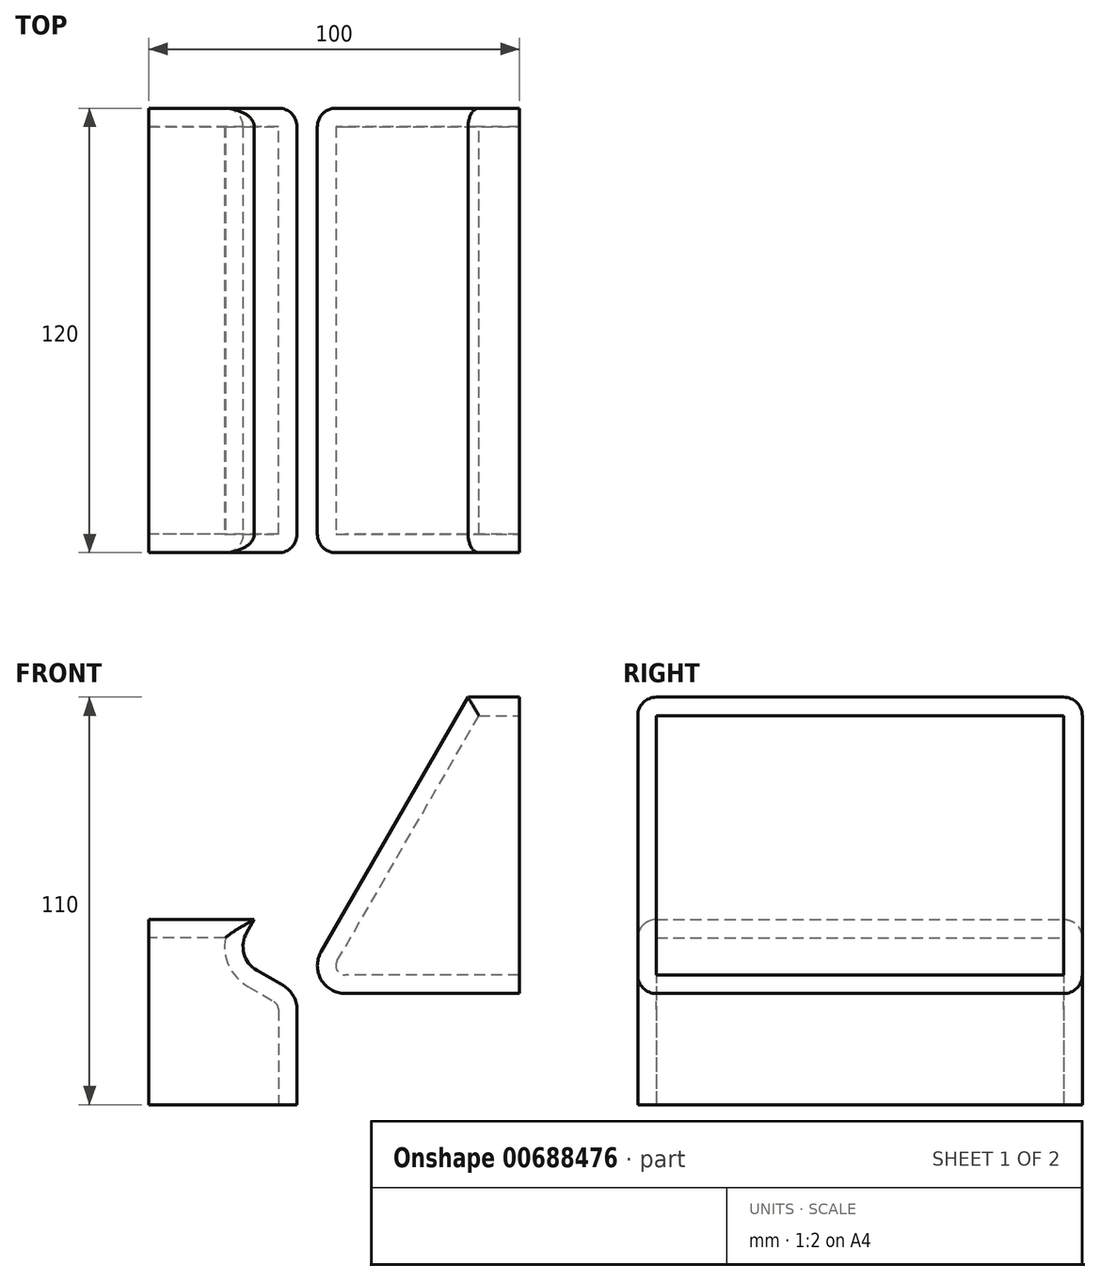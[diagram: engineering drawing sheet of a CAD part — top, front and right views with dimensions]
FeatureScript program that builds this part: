
annotation { "Feature Type Name" : "Feature", "Feature Type Description" : "" }
export const myFeature = defineFeature(function(context is Context, id is Id, definition is map)
    precondition{}
    {
        {
            var Q0;
            Q0=qCreatedBy(makeId("Front.planeOp"),FACE);
            var sketch = newSketch(context, id + "F0", { "sketchPlane" : qUnion([Q0])});
            skLineSegment(sketch, "E0.bottom", {"start": v(0, 0) * mm, "end": v(60, 0) * mm});
            skLineSegment(sketch, "E0.top", {"start": v(0, 80) * mm, "end": v(60, 80) * mm});
            skLineSegment(sketch, "E0.left", {"start": v(0, 0) * mm, "end": v(0, 80) * mm});
            skLineSegment(sketch, "E0.right", {"start": v(60, 0) * mm, "end": v(60, 80) * mm});
            skLineSegment(sketch, "E1", {"start": v(0, 0) * mm, "end": v(75, 129.9) * mm});
            skLineSegment(sketch, "E2.bottom", {"start": v(60, 0) * mm, "end": v(0, 0) * mm});
            skLineSegment(sketch, "E2.top", {"start": v(60, -30) * mm, "end": v(0, -30) * mm});
            skLineSegment(sketch, "E2.left", {"start": v(60, 0) * mm, "end": v(60, -30) * mm});
            skLineSegment(sketch, "E2.right", {"start": v(0, 0) * mm, "end": v(0, -30) * mm});
            skLineSegment(sketch, "E3.bottom", {"start": v(0, 80) * mm, "end": v(-40, 80) * mm});
            skLineSegment(sketch, "E3.top", {"start": v(0, -30) * mm, "end": v(-40, -30) * mm});
            skLineSegment(sketch, "E3.left", {"start": v(0, 80) * mm, "end": v(0, -30) * mm});
            skLineSegment(sketch, "E3.right", {"start": v(-40, 80) * mm, "end": v(-40, -30) * mm});
            skLineSegment(sketch, "E4", {"start": v(75, 129.9) * mm, "end": v(57.68, 139.9) * mm});
            skLineSegment(sketch, "E5", {"start": v(57.68, 139.9) * mm, "end": v(-17.32, 10) * mm});
            skLineSegment(sketch, "E6", {"start": v(-17.32, 10) * mm, "end": v(0, 0) * mm});
            skLineSegment(sketch, "E7", {"start": v(-40, 20) * mm, "end": v(0, 20) * mm});
            skSolve(sketch);
        }
        {
            var Q0;
            {var subQ0=sQuery(id+"F0.wireOp",EDGE,"E0.right");Q0=makeQuery(id+"F0.imprint","IMPRINT",FACE,{"disambiguationData":[TD([[makeQuery(id+"F0.imprint","IMPRINT",EDGE,{"derivedFrom":subQ0}),1.0]])]});}
            var Q1;
            {var subQ0=sQuery(id+"F0.wireOp",EDGE,"E2.bottom");Q1=makeQuery(id+"F0.imprint","IMPRINT",FACE,{"disambiguationData":[TD([[makeQuery(id+"F0.imprint","IMPRINT",EDGE,{"derivedFrom":subQ0}),1.0]])]});}
            var Q2;
            {var subQ4=sQuery(id+"F0.wireOp",EDGE,"E3.top");Q2=makeQuery(id+"F0.imprint","IMPRINT",FACE,{"disambiguationData":[TD([[makeQuery(id+"F0.imprint","IMPRINT",EDGE,{"derivedFrom":subQ4}),-1.0]])]});}
            extrude(context, id + "F1", {"entities" : qUnion([Q0, Q1, Q2]), "endBound" : BoundingType.SYMMETRIC, "depth" : 120 * mm, "offsetDistance" : 25 * mm});
        }
        {
            var Q0;
            Q0=makeQuery(id+"F1.opExtrude","SWEPT_EDGE",EDGE,{"disambiguationData":[OSD([sQuery(id+"F0.wireOp",EDGE,"E5"),sQuery(id+"F0.wireOp",EDGE,"E6")])]});
            var Q1;
            Q1=makeQuery(id+"F1.opExtrude","SWEPT_EDGE",EDGE,{"disambiguationData":[OSD([sQuery(id+"F0.wireOp",EDGE,"E1"),sQuery(id+"F0.wireOp",EDGE,"E2.bottom"),sQuery(id+"F0.wireOp",EDGE,"E3.left"),sQuery(id+"F0.wireOp",EDGE,"E6")])]});
            fillet(context, id + "F2", {"entities" : qUnion([Q0, Q1]), "radius" : 7.5 * mm, "tangentPropagation" : true, "allowEdgeOverflow" : false});
        }
        {
            var Q0;
            Q0=makeQuery(id+"F1.opExtrude","CAP_EDGE",EDGE,{"disambiguationData":[OSD([sQuery(id+"F0.wireOp",EDGE,"E0.top")])],"isStart":false});
            var Q1;
            Q1=makeQuery(id+"F1.opExtrude","CAP_EDGE",EDGE,{"disambiguationData":[OSD([sQuery(id+"F0.wireOp",EDGE,"E1")])],"isStart":false});
            var Q2;
            Q2=makeQuery(id+"F1.opExtrude","CAP_EDGE",EDGE,{"disambiguationData":[OSD([sQuery(id+"F0.wireOp",EDGE,"E6")])],"isStart":false});
            var Q3;
            Q3=makeQuery(id+"F1.opExtrude","CAP_EDGE",EDGE,{"disambiguationData":[OSD([sQuery(id+"F0.wireOp",EDGE,"E5")])],"isStart":false});
            var Q4;
            Q4=makeQuery(id+"F1.opExtrude","CAP_EDGE",EDGE,{"disambiguationData":[OSD([sQuery(id+"F0.wireOp",EDGE,"E7")])],"isStart":false});
            var Q5;
            Q5=makeQuery(id+"F1.opExtrude","CAP_EDGE",EDGE,{"disambiguationData":[OSD([sQuery(id+"F0.wireOp",EDGE,"E7")])],"isStart":true});
            var Q6;
            Q6=makeQuery(id+"F1.opExtrude","CAP_EDGE",EDGE,{"disambiguationData":[OSD([sQuery(id+"F0.wireOp",EDGE,"E1")])],"isStart":true});
            var Q7;
            Q7=makeQuery(id+"F1.opExtrude","CAP_EDGE",EDGE,{"disambiguationData":[OSD([sQuery(id+"F0.wireOp",EDGE,"E0.top")])],"isStart":true});
            var Q8;
            Q8=makeQuery(id+"F1.opExtrude","CAP_EDGE",EDGE,{"disambiguationData":[OSD([sQuery(id+"F0.wireOp",EDGE,"E6")])],"isStart":true});
            var Q9;
            Q9=makeQuery(id+"F1.opExtrude","CAP_EDGE",EDGE,{"disambiguationData":[OSD([sQuery(id+"F0.wireOp",EDGE,"E5")])],"isStart":true});
            fillet(context, id + "F3", {"entities" : qUnion([Q0, Q1, Q2, Q3, Q4, Q5, Q6, Q7, Q8, Q9]), "radius" : 5 * mm, "tangentPropagation" : true, "allowEdgeOverflow" : false});
        }
        {
            var Q0;
            Q0=makeQuery(id+"F1.opExtrude","SWEPT_FACE",FACE,{"disambiguationData":[OSD([sQuery(id+"F0.wireOp",EDGE,"E3.right")])]});
            var Q1;
            Q1=makeQuery(id+"F1.opExtrude","SWEPT_FACE",FACE,{"disambiguationData":[OSD([sQuery(id+"F0.wireOp",EDGE,"E0.right"),sQuery(id+"F0.wireOp",EDGE,"E2.left")])]});
            var Q2;
            Q2=makeQuery(id+"F1.opExtrude","SWEPT_FACE",FACE,{"disambiguationData":[OSD([sQuery(id+"F0.wireOp",EDGE,"E2.top"),sQuery(id+"F0.wireOp",EDGE,"E3.top")])]});
            shell(context, id + "F4", {"entities" : qUnion([Q0, Q1, Q2]), "thickness" : 5 * mm});
        }
    });
